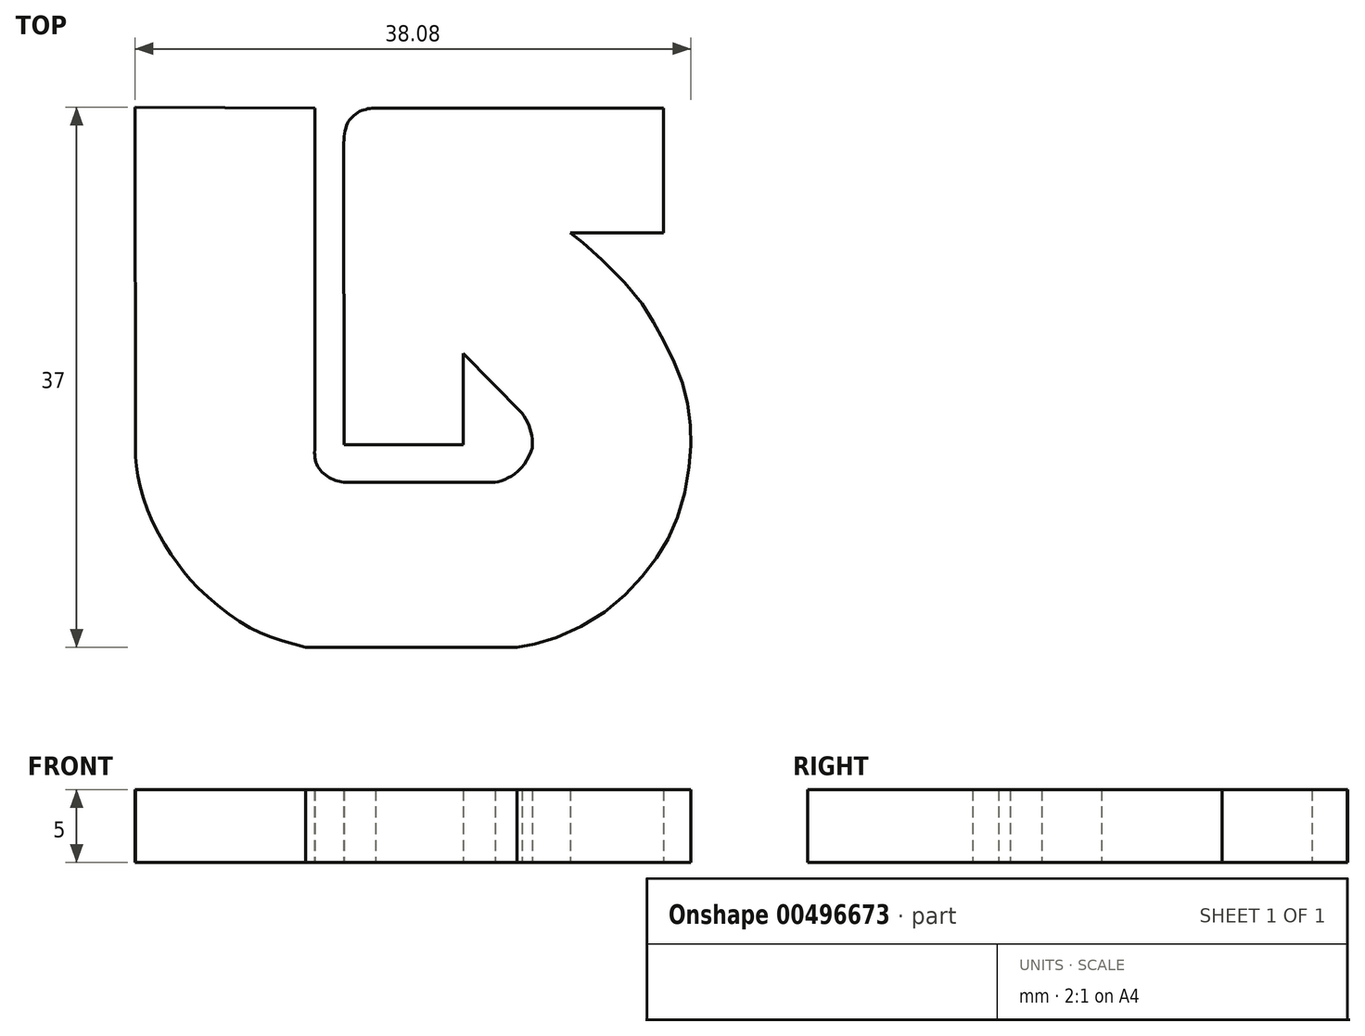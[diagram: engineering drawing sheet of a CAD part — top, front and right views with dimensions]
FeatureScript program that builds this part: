
annotation { "Feature Type Name" : "Feature", "Feature Type Description" : "" }
export const myFeature = defineFeature(function(context is Context, id is Id, definition is map)
    precondition{}
    {
        {
            var Q0;
            Q0=qCreatedBy(makeId("Top.planeOp"),FACE);
            var sketch = newSketch(context, id + "F0", { "sketchPlane" : qUnion([Q0])});
            skFitSpline(sketch, "E0", {"points": [v(-1.06, 28.8) * mm, v(-1.02, 4.86) * mm], "startDerivative": vector(0.04, -23.93) * mm, "endDerivative": vector(0.04, -23.93) * mm});
            skFitSpline(sketch, "E1", {"points": [v(-1.02, 4.86) * mm, v(-0.75, 2.99) * mm, v(0.27, 0.12) * mm, v(1.73, -2.28) * mm, v(3.06, -3.92) * mm, v(5.6, -6.09) * mm, v(8.08, -7.43) * mm, v(10.62, -8.2) * mm], "startDerivative": vector(1.32, -14.67) * mm, "endDerivative": vector(18.05, -4.68) * mm});
            skFitSpline(sketch, "E2", {"points": [v(10.62, -8.2) * mm, v(25.12, -8.2) * mm], "startDerivative": vector(14.5, 0) * mm, "endDerivative": vector(14.5, 0) * mm});
            skFitSpline(sketch, "E3", {"points": [v(25.12, -8.2) * mm, v(26.92, -7.82) * mm, v(30.26, -6.35) * mm, v(33.1, -4) * mm, v(34.9, -1.7) * mm, v(36.13, 0.75) * mm, v(36.9, 4.17) * mm, v(37, 6.51) * mm, v(36.7, 8.85) * mm, v(35.92, 11.23) * mm, v(34.62, 13.74) * mm, v(33.28, 15.86) * mm, v(29.95, 19.24) * mm, v(28.77, 20.2) * mm], "startDerivative": vector(26.55, 4.2) * mm, "endDerivative": vector(-17.38, 13.18) * mm});
            skFitSpline(sketch, "E4", {"points": [v(28.77, 20.2) * mm, v(35.13, 20.2) * mm], "startDerivative": vector(6.36, 0) * mm, "endDerivative": vector(6.36, 0) * mm});
            skFitSpline(sketch, "E5", {"points": [v(35.13, 20.2) * mm, v(35.13, 28.74) * mm], "startDerivative": vector(0, 8.54) * mm, "endDerivative": vector(0, 8.54) * mm});
            skFitSpline(sketch, "E6", {"points": [v(35.13, 28.74) * mm, v(15.42, 28.74) * mm], "startDerivative": vector(-19.7, 0) * mm, "endDerivative": vector(-19.7, 0) * mm});
            skFitSpline(sketch, "E7", {"points": [v(15.42, 28.74) * mm, v(14.9, 28.68) * mm, v(14.27, 28.46) * mm, v(13.75, 28.05) * mm, v(13.43, 27.52) * mm, v(13.23, 26.34) * mm], "startDerivative": vector(-2.93, -0.2) * mm, "endDerivative": vector(-0.54, -5.05) * mm});
            skFitSpline(sketch, "E8", {"points": [v(13.23, 26.34) * mm, v(13.28, 5.66) * mm], "startDerivative": vector(0.05, -20.67) * mm, "endDerivative": vector(0.05, -20.67) * mm});
            skFitSpline(sketch, "E9", {"points": [v(13.28, 5.66) * mm, v(21.44, 5.66) * mm], "startDerivative": vector(8.16, 0) * mm, "endDerivative": vector(8.16, 0) * mm});
            skFitSpline(sketch, "E10", {"points": [v(21.44, 5.66) * mm, v(21.44, 11.94) * mm], "startDerivative": vector(0, 6.27) * mm, "endDerivative": vector(0, 6.27) * mm});
            skFitSpline(sketch, "E11", {"points": [v(21.44, 11.94) * mm, v(25.44, 7.83) * mm], "startDerivative": vector(4, -4.11) * mm, "endDerivative": vector(4, -4.11) * mm});
            skFitSpline(sketch, "E12", {"points": [v(25.44, 7.83) * mm, v(25.7, 7.45) * mm, v(25.93, 7) * mm, v(26.05, 6.58) * mm, v(26.14, 6.14) * mm, v(26.14, 5.49) * mm, v(25.92, 4.86) * mm, v(25.44, 4.13) * mm, v(24.92, 3.63) * mm, v(24.46, 3.38) * mm, v(23.96, 3.16) * mm, v(23.6, 3.09) * mm], "startDerivative": vector(3.2, -4.4) * mm, "endDerivative": vector(-4.63, -0.65) * mm});
            skFitSpline(sketch, "E13", {"points": [v(23.6, 3.09) * mm, v(13.23, 3.09) * mm], "startDerivative": vector(-10.38, 0) * mm, "endDerivative": vector(-10.38, 0) * mm});
            skFitSpline(sketch, "E14", {"points": [v(13.23, 3.09) * mm, v(12.47, 3.32) * mm, v(11.74, 3.8) * mm, v(11.3, 4.59) * mm, v(11.27, 5.66) * mm], "startDerivative": vector(-3.27, 0.77) * mm, "endDerivative": vector(0.24, 4.1) * mm});
            skFitSpline(sketch, "E15", {"points": [v(11.27, 5.66) * mm, v(11.27, 28.74) * mm], "startDerivative": vector(0, 23.07) * mm, "endDerivative": vector(0, 23.07) * mm});
            skFitSpline(sketch, "E16", {"points": [v(11.27, 28.74) * mm, v(-1.06, 28.8) * mm], "startDerivative": vector(-12.33, 0.06) * mm, "endDerivative": vector(-12.33, 0.06) * mm});
            skSolve(sketch);
        }
        {
            var Q0;
            Q0 = qSketchRegion(id + "F0", true);
            extrude(context, id + "F1", {"entities" : qUnion([Q0]), "depth" : 5 * mm, "offsetDistance" : 25 * mm});
        }
    });
